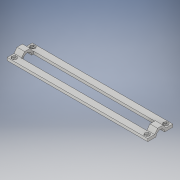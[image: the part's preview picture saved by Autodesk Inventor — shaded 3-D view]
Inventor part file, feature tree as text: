
AUTODESK INVENTOR PART (.ipt)
format: ipt  version: 2019 (Build 230136000, 136)  size: 297,472 bytes
history: native  units: mm
features: extrude x11, sketch x11, projected_geometry x3, thicken_offset x2
ambient origin geometry x8: Origin, YZ Plane, XZ Plane, XY Plane, X Axis, Y Axis, Z Axis, Center Point
bodies: Solid1 (feature_tree)
feature tree (27):
  extrude  "Extrusion1"  Depth=7.0mm
  extrude  "Extrusion2"  Depth=1.5mm
  extrude  "Extrusion3"  Depth=1.5mm TaperAngle=0.0deg
  extrude  "Extrusion4"  Depth=3.0mm
  extrude  "Extrusion5"  Depth=3.5mm TaperAngle=0.0deg
  extrude  "Extrusion6"  Depth=6.0mm TaperAngle=0.0deg
  extrude  "Extrusion7"  Depth=3.0mm
  extrude  "Extrusion8"  Depth=2.0mm
  extrude  "Extrusion9"  Depth=7.0mm
  extrude  "Extrusion10"  Depth=3.5mm
  extrude  "Extrusion11"  Depth=1.0mm
  thicken_offset  "Thicken1"
  thicken_offset  "Thicken2"
  sketch  "Sketch1"  dims[d0=5.0mm d1=7.0mm]
  sketch  "Sketch2"  dims[d2=50.0mm d3=0.0mm d4=1.5mm]
  sketch  "Sketch3"  dims[d5=1.5mm d6=6.0mm d7=0.0mm]
  sketch  "Sketch4"  dims[d8=2.0mm d9=3.0mm]
  sketch  "Sketch6"  dims[d10=3.5mm d11=6.0mm d12=0.0mm]
  sketch  "Sketch7"  dims[d21=8.0mm d22=6.0mm d23=0.0mm]
  sketch  "Sketch8"  dims[d26=3.0mm d27=3.0mm]
  sketch  "Sketch9"  dims[d28=8.0mm d29=2.0mm]
  projected_geometry  "Projected Loop1"
  sketch  "Sketch10"  dims[d30=7.0mm d31=0.0mm d32=2.0mm]
  sketch  "Sketch11"  dims[d33=3.0mm d34=3.5mm]
  projected_geometry  "Projected Loop2"
  projected_geometry  "Projected Loop3"
  sketch  "Sketch12"  dims[d35=3.5mm d36=3.0mm d37=2.0mm d38=7.0mm d39=0.0mm d40=10.0mm d41=0.0mm d42=121.4mm d43=0.0mm d44=2.0mm d45=2.0mm d46=3.5mm d47=3.5mm d48=3.0mm d49=3.0mm d50=121.4mm d51=0.0mm d52=4.1mm d53=4.1mm d54=4.1mm d55=4.1mm d56=1.0mm d57=0.0mm d58=7.0mm d59=7.0mm d60=1.0mm d61=0.0mm d62=0.5mm d63=0.5mm d64=0.5mm d65=0.5mm]
